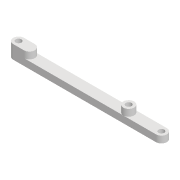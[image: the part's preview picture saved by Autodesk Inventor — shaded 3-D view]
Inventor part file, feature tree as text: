
AUTODESK INVENTOR PART (.ipt)
format: ipt  version: 2022 (Build 260153000, 153)  size: 119,808 bytes
history: native  units: mm
features: extrude x2, sketch x1, projected_geometry x1
ambient origin geometry x8: Origin, YZ Plane, XZ Plane, XY Plane, X Axis, Y Axis, Z Axis, Center Point
bodies: Solid1 (feature_tree)
feature tree (4):
  extrude  "Extrusion1"  Depth=8.0mm
  extrude  "Extrusion7"  Depth=5.0mm
  sketch  "Sketch2"  dims[d0=105.445mm d1=8.0mm d2=4.2mm d4=5.0mm d5=0.0mm d8=4.2mm d9=81.271mm d10=4.2mm d11=8.0mm d12=8.0mm d13=8.0mm d28=8.0mm d33=5.0mm d34=0.0mm]
  projected_geometry  "Projected Loop1"
